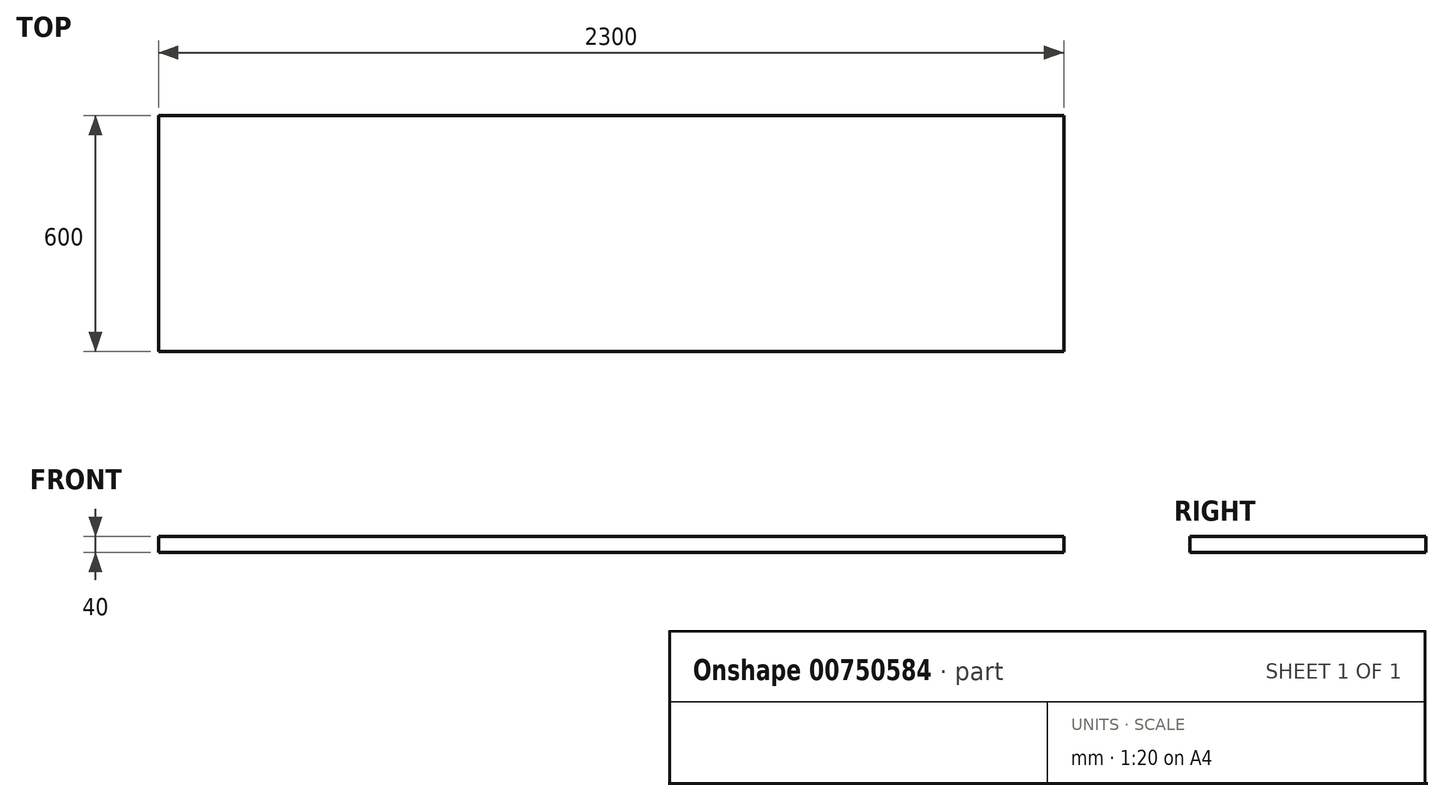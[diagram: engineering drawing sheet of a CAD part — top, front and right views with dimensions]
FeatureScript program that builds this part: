
annotation { "Feature Type Name" : "Feature", "Feature Type Description" : "" }
export const myFeature = defineFeature(function(context is Context, id is Id, definition is map)
    precondition{}
    {
        {
            var Q0;
            Q0=qCreatedBy(makeId("Top.planeOp"),FACE);
            var sketch = newSketch(context, id + "F0", { "sketchPlane" : qUnion([Q0])});
            skLineSegment(sketch, "E0.bottom", {"start": v(1150, -300) * mm, "end": v(-1150, -300) * mm});
            skLineSegment(sketch, "E0.top", {"start": v(1150, 300) * mm, "end": v(-1150, 300) * mm});
            skLineSegment(sketch, "E0.left", {"start": v(1150, -300) * mm, "end": v(1150, 300) * mm});
            skLineSegment(sketch, "E0.right", {"start": v(-1150, -300) * mm, "end": v(-1150, 300) * mm});
            skPoint(sketch, "E0.middle", {"position": v(0, 0) * mm});
            skSolve(sketch);
        }
        {
            var Q0;
            Q0=qSketchRegion(id+"F0",true);
            extrude(context, id + "F1", {"entities" : qUnion([Q0]), "depth" : 40 * mm, "offsetDistance" : 25 * mm});
        }
    });
